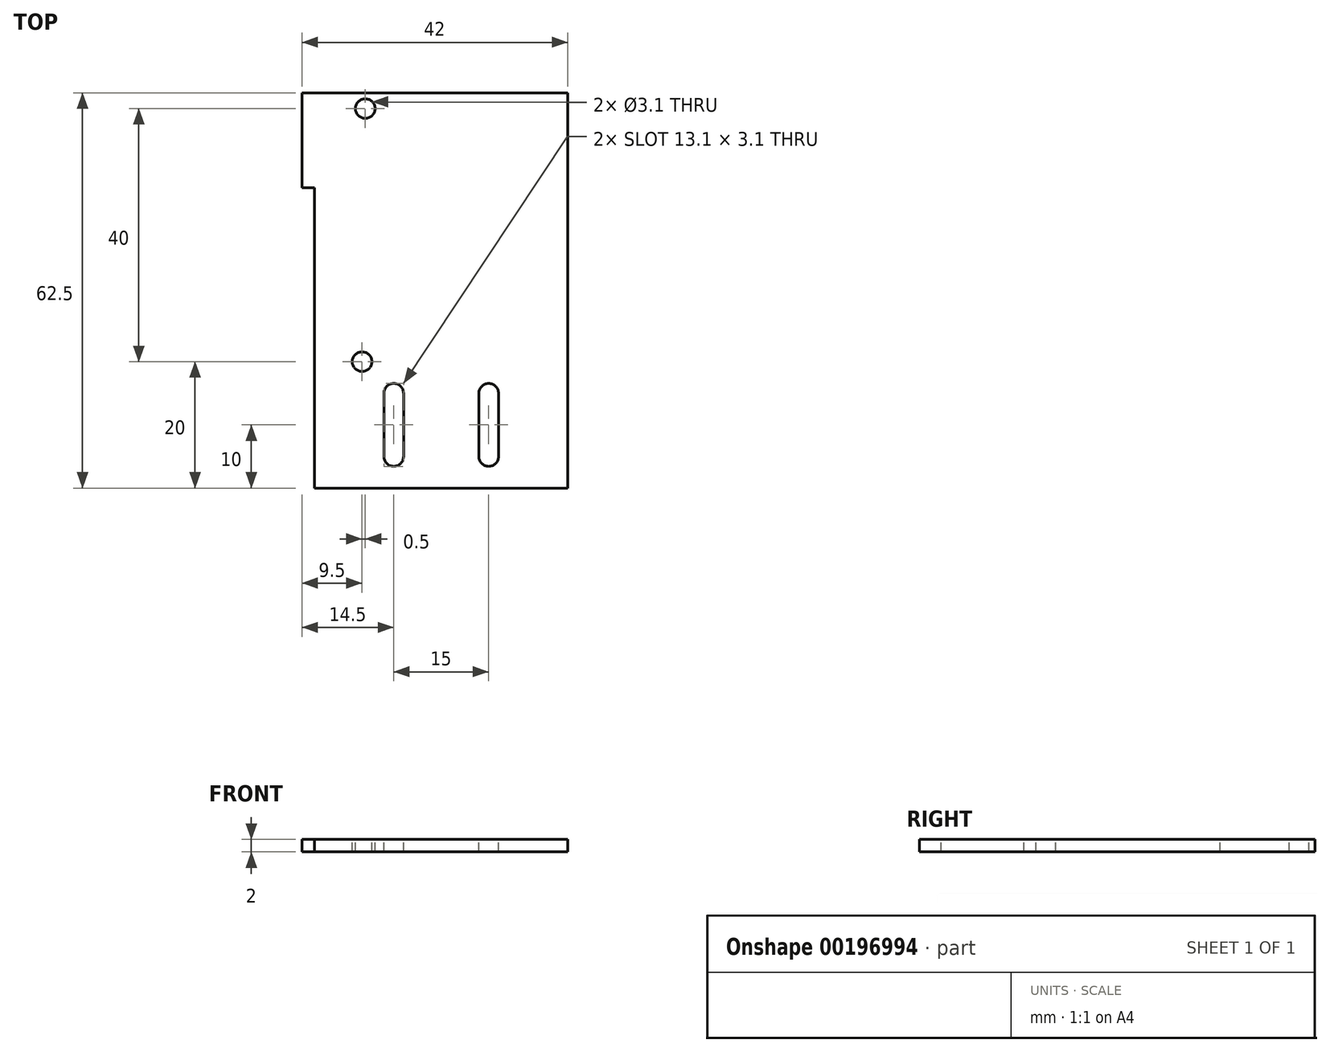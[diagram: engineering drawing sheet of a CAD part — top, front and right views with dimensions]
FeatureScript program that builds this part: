
annotation { "Feature Type Name" : "Feature", "Feature Type Description" : "" }
export const myFeature = defineFeature(function(context is Context, id is Id, definition is map)
    precondition{}
    {
        {
            var Q0;
            Q0=qCreatedBy(makeId("Top.planeOp"),FACE);
            var sketch = newSketch(context, id + "F0", { "sketchPlane" : qUnion([Q0])});
            skLineSegment(sketch, "E0.bottom", {"start": v(20, 32.5) * mm, "end": v(-20, 32.5) * mm});
            skLineSegment(sketch, "E0.top", {"start": v(20, -32.5) * mm, "end": v(-20, -32.5) * mm});
            skLineSegment(sketch, "E0.left", {"start": v(20, 32.5) * mm, "end": v(20, -32.5) * mm});
            skLineSegment(sketch, "E0.right", {"start": v(-20, 32.5) * mm, "end": v(-20, -32.5) * mm});
            skPoint(sketch, "E0.middle", {"position": v(0, 0) * mm});
            skSolve(sketch);
        }
        {
            var Q0;
            Q0 = qSketchRegion(id + "F0", true);
            extrude(context, id + "F1", {"entities" : qUnion([Q0]), "depth" : 2 * mm});
        }
        {
            var Q0;
            Q0=makeQuery(id+"F1.opExtrude","CAP_FACE",FACE,{"disambiguationData":[OSD([sQuery(id+"F0.wireOp",EDGE,"E0.bottom"),sQuery(id+"F0.wireOp",EDGE,"E0.top"),sQuery(id+"F0.wireOp",EDGE,"E0.left"),sQuery(id+"F0.wireOp",EDGE,"E0.right")])],"isStart":false});
            var sketch = newSketch(context, id + "F2", { "sketchPlane" : qUnion([Q0])});
            skLineSegment(sketch, "E1", {"start": v(0, 0) * mm, "end": v(0, 20) * mm, "construction": true});
            skLineSegment(sketch, "E2", {"start": v(0, 20) * mm, "end": v(-20, 20) * mm, "construction": true});
            skLineSegment(sketch, "E3.bottom", {"start": v(-20, 12.5) * mm, "end": v(-22, 12.5) * mm});
            skLineSegment(sketch, "E3.top", {"start": v(-20, 27.5) * mm, "end": v(-22, 27.5) * mm});
            skLineSegment(sketch, "E3.left", {"start": v(-20, 12.5) * mm, "end": v(-20, 27.5) * mm});
            skLineSegment(sketch, "E3.right", {"start": v(-22, 12.5) * mm, "end": v(-22, 27.5) * mm});
            skSolve(sketch);
        }
        {
            var Q0;
            Q0 = qSketchRegion(id + "F2", true);
            extrude(context, id + "F3", {"entities" : qUnion([Q0]), "operationType" : NewBodyOperationType.ADD, "oppositeDirection" : true, "depth" : 2 * mm});
        }
        {
            var Q0;
            {var subQ0=sQuery(id+"F2.wireOp",EDGE,"E3.right");var subQ1=sQuery(id+"F2.wireOp",EDGE,"E3.left");var subQ2=sQuery(id+"F2.wireOp",EDGE,"E3.top");var subQ3=sQuery(id+"F2.wireOp",EDGE,"E3.bottom");Q0=makeQuery(id+"FAu347zrFNA7xFl_1.1.FN0kvEoHNVdJmEl_1.1.F3.boolean.opBoolean","MERGE",FACE,{"derivedFrom":[makeQuery(id+"FAu347zrFNA7xFl_1.1.F3.boolean.opBoolean","MERGE",FACE,{"derivedFrom":[makeQuery(id+"FN0kvEoHNVdJmEl_1.1.F3.boolean.opBoolean","MERGE",FACE,{"derivedFrom":[makeQuery(id+"F3.boolean.opBoolean","MERGE",FACE,{"derivedFrom":[makeQuery(id+"F1.opExtrude","CAP_FACE",FACE,{"disambiguationData":[OSD([sQuery(id+"F0.wireOp",EDGE,"E0.bottom"),sQuery(id+"F0.wireOp",EDGE,"E0.top"),sQuery(id+"F0.wireOp",EDGE,"E0.left"),sQuery(id+"F0.wireOp",EDGE,"E0.right")])],"isStart":false}),makeQuery(id+"F3.opExtrude","CAP_FACE",FACE,{"disambiguationData":[OSD([subQ3,subQ2,subQ1,subQ0])],"isStart":true})]}),makeQuery(id+"FN0kvEoHNVdJmEl_1.1.F3.opExtrude","CAP_FACE",FACE,{"disambiguationData":[OSD([subQ3,subQ2,subQ1,subQ0])],"isStart":true})]}),makeQuery(id+"FAu347zrFNA7xFl_1.1.F3.opExtrude","CAP_FACE",FACE,{"disambiguationData":[OSD([subQ3,subQ2,subQ1,subQ0])],"isStart":true})]}),makeQuery(id+"FAu347zrFNA7xFl_1.1.FN0kvEoHNVdJmEl_1.1.F3.opExtrude","CAP_FACE",FACE,{"disambiguationData":[OSD([subQ3,subQ2,subQ1,subQ0])],"isStart":true})]});}
            var sketch = newSketch(context, id + "F4", { "sketchPlane" : qUnion([Q0])});
            skLineSegment(sketch, "E4", {"start": v(0, 0) * mm, "end": v(0, 25) * mm, "construction": true});
            skLineSegment(sketch, "E5", {"start": v(0, 25) * mm, "end": v(-12, 25) * mm, "construction": true});
            skCircle(sketch, "E6", {"center": v(-12, 25) * mm, "radius": 1.55 * mm});
            skSolve(sketch);
        }
        {
            var Q0;
            Q0 = qSketchRegion(id + "F4", true);
            extrude(context, id + "F5", {"entities" : qUnion([Q0]), "operationType" : NewBodyOperationType.REMOVE, "endBound" : BoundingType.THROUGH_ALL, "oppositeDirection" : true, "depth" : 25 * mm});
        }
        {
            var Q0;
            {var subQ0=sQuery(id+"F2.wireOp",EDGE,"E3.right");var subQ1=sQuery(id+"F2.wireOp",EDGE,"E3.left");var subQ2=sQuery(id+"F2.wireOp",EDGE,"E3.top");var subQ3=sQuery(id+"F2.wireOp",EDGE,"E3.bottom");Q0=makeQuery(id+"FAu347zrFNA7xFl_1.1.FN0kvEoHNVdJmEl_1.1.F3.boolean.opBoolean","MERGE",FACE,{"derivedFrom":[makeQuery(id+"FAu347zrFNA7xFl_1.1.F3.boolean.opBoolean","MERGE",FACE,{"derivedFrom":[makeQuery(id+"FN0kvEoHNVdJmEl_1.1.F3.boolean.opBoolean","MERGE",FACE,{"derivedFrom":[makeQuery(id+"F3.boolean.opBoolean","MERGE",FACE,{"derivedFrom":[makeQuery(id+"F1.opExtrude","CAP_FACE",FACE,{"disambiguationData":[OSD([sQuery(id+"F0.wireOp",EDGE,"E0.bottom"),sQuery(id+"F0.wireOp",EDGE,"E0.top"),sQuery(id+"F0.wireOp",EDGE,"E0.left"),sQuery(id+"F0.wireOp",EDGE,"E0.right")])],"isStart":false}),makeQuery(id+"F3.opExtrude","CAP_FACE",FACE,{"disambiguationData":[OSD([subQ3,subQ2,subQ1,subQ0])],"isStart":true})]}),makeQuery(id+"FN0kvEoHNVdJmEl_1.1.F3.opExtrude","CAP_FACE",FACE,{"disambiguationData":[OSD([subQ3,subQ2,subQ1,subQ0])],"isStart":true})]}),makeQuery(id+"FAu347zrFNA7xFl_1.1.F3.opExtrude","CAP_FACE",FACE,{"disambiguationData":[OSD([subQ3,subQ2,subQ1,subQ0])],"isStart":true})]}),makeQuery(id+"FAu347zrFNA7xFl_1.1.FN0kvEoHNVdJmEl_1.1.F3.opExtrude","CAP_FACE",FACE,{"disambiguationData":[OSD([subQ3,subQ2,subQ1,subQ0])],"isStart":true})]});}
            var sketch = newSketch(context, id + "F6", { "sketchPlane" : qUnion([Q0])});
            skLineSegment(sketch, "E7", {"start": v(0, 0) * mm, "end": v(0, -30) * mm, "construction": true});
            skLineSegment(sketch, "E8", {"start": v(0, -30) * mm, "end": v(7.5, -30) * mm, "construction": true});
            skLineSegment(sketch, "E9", {"start": v(0, -30) * mm, "end": v(-7.5, -30) * mm, "construction": true});
            skArc(sketch, "E10", {"start": v(-9.05, -30) * mm, "mid": v(-7.5, -31.55) * mm, "end": v(-5.95, -30) * mm});
            skArc(sketch, "E11", {"start": v(5.95, -30) * mm, "mid": v(7.5, -31.55) * mm, "end": v(9.05, -30) * mm});
            skLineSegment(sketch, "E12", {"start": v(-7.5, -30) * mm, "end": v(-7.5, -20) * mm, "construction": true});
            skLineSegment(sketch, "E13", {"start": v(7.5, -30) * mm, "end": v(7.5, -20) * mm, "construction": true});
            skArc(sketch, "E14", {"start": v(9.05, -20) * mm, "mid": v(7.5, -18.45) * mm, "end": v(5.95, -20) * mm});
            skArc(sketch, "E15", {"start": v(-5.95, -20) * mm, "mid": v(-7.5, -18.45) * mm, "end": v(-9.05, -20) * mm});
            skLineSegment(sketch, "E16", {"start": v(-5.95, -20) * mm, "end": v(-9.05, -20) * mm, "construction": true});
            skLineSegment(sketch, "E17", {"start": v(5.95, -20) * mm, "end": v(9.05, -20) * mm, "construction": true});
            skLineSegment(sketch, "E18", {"start": v(9.05, -30) * mm, "end": v(7.5, -30) * mm, "construction": true});
            skLineSegment(sketch, "E19", {"start": v(-7.5, -30) * mm, "end": v(-9.05, -30) * mm, "construction": true});
            skLineSegment(sketch, "E20", {"start": v(-9.05, -20) * mm, "end": v(-9.05, -30) * mm});
            skLineSegment(sketch, "E21", {"start": v(-7.5, -30) * mm, "end": v(-5.95, -30) * mm, "construction": true});
            skLineSegment(sketch, "E22", {"start": v(7.5, -30) * mm, "end": v(5.95, -30) * mm, "construction": true});
            skLineSegment(sketch, "E23", {"start": v(5.95, -20) * mm, "end": v(5.95, -30) * mm});
            skLineSegment(sketch, "E24", {"start": v(9.05, -20) * mm, "end": v(9.05, -30) * mm});
            skLineSegment(sketch, "E25", {"start": v(-5.95, -20) * mm, "end": v(-5.95, -30) * mm});
            skSolve(sketch);
        }
        {
            var Q0;
            Q0 = qSketchRegion(id + "F6", true);
            extrude(context, id + "F7", {"entities" : qUnion([Q0]), "operationType" : NewBodyOperationType.REMOVE, "endBound" : BoundingType.THROUGH_ALL, "oppositeDirection" : true, "depth" : 25 * mm});
        }
        {
            var Q0;
            {var subQ0=sQuery(id+"F2.wireOp",EDGE,"E3.right");var subQ1=sQuery(id+"F2.wireOp",EDGE,"E3.left");var subQ2=sQuery(id+"F2.wireOp",EDGE,"E3.top");var subQ3=sQuery(id+"F2.wireOp",EDGE,"E3.bottom");Q0=makeQuery(id+"FAu347zrFNA7xFl_1.1.FN0kvEoHNVdJmEl_1.1.F3.boolean.opBoolean","MERGE",FACE,{"derivedFrom":[makeQuery(id+"FAu347zrFNA7xFl_1.1.F3.boolean.opBoolean","MERGE",FACE,{"derivedFrom":[makeQuery(id+"FN0kvEoHNVdJmEl_1.1.F3.boolean.opBoolean","MERGE",FACE,{"derivedFrom":[makeQuery(id+"F3.boolean.opBoolean","MERGE",FACE,{"derivedFrom":[makeQuery(id+"F1.opExtrude","CAP_FACE",FACE,{"disambiguationData":[OSD([sQuery(id+"F0.wireOp",EDGE,"E0.bottom"),sQuery(id+"F0.wireOp",EDGE,"E0.top"),sQuery(id+"F0.wireOp",EDGE,"E0.left"),sQuery(id+"F0.wireOp",EDGE,"E0.right")])],"isStart":false}),makeQuery(id+"F3.opExtrude","CAP_FACE",FACE,{"disambiguationData":[OSD([subQ3,subQ2,subQ1,subQ0])],"isStart":true})]}),makeQuery(id+"FN0kvEoHNVdJmEl_1.1.F3.opExtrude","CAP_FACE",FACE,{"disambiguationData":[OSD([subQ3,subQ2,subQ1,subQ0])],"isStart":true})]}),makeQuery(id+"FAu347zrFNA7xFl_1.1.F3.opExtrude","CAP_FACE",FACE,{"disambiguationData":[OSD([subQ3,subQ2,subQ1,subQ0])],"isStart":true})]}),makeQuery(id+"FAu347zrFNA7xFl_1.1.FN0kvEoHNVdJmEl_1.1.F3.opExtrude","CAP_FACE",FACE,{"disambiguationData":[OSD([subQ3,subQ2,subQ1,subQ0])],"isStart":true})]});}
            var sketch = newSketch(context, id + "F8", { "sketchPlane" : qUnion([Q0])});
            skLineSegment(sketch, "E26.bottom", {"start": v(-20, -32.5) * mm, "end": v(20, -32.5) * mm});
            skLineSegment(sketch, "E26.top", {"start": v(-20, -35) * mm, "end": v(20, -35) * mm});
            skLineSegment(sketch, "E26.left", {"start": v(-20, -32.5) * mm, "end": v(-20, -35) * mm});
            skLineSegment(sketch, "E26.right", {"start": v(20, -32.5) * mm, "end": v(20, -35) * mm});
            skSolve(sketch);
        }
        {
            var Q0;
            Q0 = qSketchRegion(id + "F8", true);
            var Q1;
            {var subQ0=sQuery(id+"F2.wireOp",EDGE,"E3.right");var subQ1=sQuery(id+"F2.wireOp",EDGE,"E3.left");var subQ2=sQuery(id+"F2.wireOp",EDGE,"E3.top");var subQ3=sQuery(id+"F2.wireOp",EDGE,"E3.bottom");Q1=makeQuery(id+"FAu347zrFNA7xFl_1.1.FN0kvEoHNVdJmEl_1.1.F3.boolean.opBoolean","MERGE",FACE,{"derivedFrom":[makeQuery(id+"FAu347zrFNA7xFl_1.1.F3.boolean.opBoolean","MERGE",FACE,{"derivedFrom":[makeQuery(id+"FN0kvEoHNVdJmEl_1.1.F3.boolean.opBoolean","MERGE",FACE,{"derivedFrom":[makeQuery(id+"F3.boolean.opBoolean","MERGE",FACE,{"derivedFrom":[makeQuery(id+"F1.opExtrude","CAP_FACE",FACE,{"disambiguationData":[OSD([sQuery(id+"F0.wireOp",EDGE,"E0.bottom"),sQuery(id+"F0.wireOp",EDGE,"E0.top"),sQuery(id+"F0.wireOp",EDGE,"E0.left"),sQuery(id+"F0.wireOp",EDGE,"E0.right")])],"isStart":true}),makeQuery(id+"F3.opExtrude","CAP_FACE",FACE,{"disambiguationData":[OSD([subQ3,subQ2,subQ1,subQ0])],"isStart":false})]}),makeQuery(id+"FN0kvEoHNVdJmEl_1.1.F3.opExtrude","CAP_FACE",FACE,{"disambiguationData":[OSD([subQ3,subQ2,subQ1,subQ0])],"isStart":false})]}),makeQuery(id+"FAu347zrFNA7xFl_1.1.F3.opExtrude","CAP_FACE",FACE,{"disambiguationData":[OSD([subQ3,subQ2,subQ1,subQ0])],"isStart":false})]}),makeQuery(id+"FAu347zrFNA7xFl_1.1.FN0kvEoHNVdJmEl_1.1.F3.opExtrude","CAP_FACE",FACE,{"disambiguationData":[OSD([subQ3,subQ2,subQ1,subQ0])],"isStart":false})]});}
            extrude(context, id + "F9", {"entities" : qUnion([Q0]), "operationType" : NewBodyOperationType.ADD, "endBound" : BoundingType.UP_TO_SURFACE, "oppositeDirection" : true, "endBoundEntityFace" : qUnion([Q1]), "depth" : 2 * mm});
        }
        {
            var Q0;
            {var subQ0=sQuery(id+"F2.wireOp",EDGE,"E3.right");var subQ1=sQuery(id+"F2.wireOp",EDGE,"E3.left");var subQ2=sQuery(id+"F2.wireOp",EDGE,"E3.top");var subQ3=sQuery(id+"F2.wireOp",EDGE,"E3.bottom");Q0=makeQuery(id+"F9.boolean.opBoolean","MERGE",FACE,{"derivedFrom":[makeQuery(id+"FAu347zrFNA7xFl_1.1.FN0kvEoHNVdJmEl_1.1.F3.boolean.opBoolean","MERGE",FACE,{"derivedFrom":[makeQuery(id+"FAu347zrFNA7xFl_1.1.F3.boolean.opBoolean","MERGE",FACE,{"derivedFrom":[makeQuery(id+"FN0kvEoHNVdJmEl_1.1.F3.boolean.opBoolean","MERGE",FACE,{"derivedFrom":[makeQuery(id+"F3.boolean.opBoolean","MERGE",FACE,{"derivedFrom":[makeQuery(id+"F1.opExtrude","CAP_FACE",FACE,{"disambiguationData":[OSD([sQuery(id+"F0.wireOp",EDGE,"E0.bottom"),sQuery(id+"F0.wireOp",EDGE,"E0.top"),sQuery(id+"F0.wireOp",EDGE,"E0.left"),sQuery(id+"F0.wireOp",EDGE,"E0.right")])],"isStart":false}),makeQuery(id+"F3.opExtrude","CAP_FACE",FACE,{"disambiguationData":[OSD([subQ3,subQ2,subQ1,subQ0])],"isStart":true})]}),makeQuery(id+"FN0kvEoHNVdJmEl_1.1.F3.opExtrude","CAP_FACE",FACE,{"disambiguationData":[OSD([subQ3,subQ2,subQ1,subQ0])],"isStart":true})]}),makeQuery(id+"FAu347zrFNA7xFl_1.1.F3.opExtrude","CAP_FACE",FACE,{"disambiguationData":[OSD([subQ3,subQ2,subQ1,subQ0])],"isStart":true})]}),makeQuery(id+"FAu347zrFNA7xFl_1.1.FN0kvEoHNVdJmEl_1.1.F3.opExtrude","CAP_FACE",FACE,{"disambiguationData":[OSD([subQ3,subQ2,subQ1,subQ0])],"isStart":true})]}),makeQuery(id+"F9.opExtrude","CAP_FACE",FACE,{"disambiguationData":[OSD([sQuery(id+"F8.wireOp",EDGE,"E26.bottom"),sQuery(id+"F8.wireOp",EDGE,"E26.top"),sQuery(id+"F8.wireOp",EDGE,"E26.left"),sQuery(id+"F8.wireOp",EDGE,"E26.right")])],"isStart":true})]});}
            var sketch = newSketch(context, id + "F10", { "sketchPlane" : qUnion([Q0])});
            skCircle(sketch, "E27", {"center": v(-12.5, -15) * mm, "radius": 1.55 * mm});
            skLineSegment(sketch, "E28", {"start": v(-12.5, -15) * mm, "end": v(0, -15) * mm, "construction": true});
            skLineSegment(sketch, "E29", {"start": v(0, -15) * mm, "end": v(0, 0) * mm, "construction": true});
            skSolve(sketch);
        }
        {
            var Q0;
            Q0 = qSketchRegion(id + "F10", true);
            extrude(context, id + "F11", {"entities" : qUnion([Q0]), "operationType" : NewBodyOperationType.REMOVE, "endBound" : BoundingType.THROUGH_ALL, "oppositeDirection" : true, "depth" : 25 * mm});
        }
        {
            var Q0;
            {var subQ0=sQuery(id+"F2.wireOp",EDGE,"E3.right");var subQ1=sQuery(id+"F2.wireOp",EDGE,"E3.left");var subQ2=sQuery(id+"F2.wireOp",EDGE,"E3.top");var subQ3=sQuery(id+"F2.wireOp",EDGE,"E3.bottom");Q0=makeQuery(id+"F9.boolean.opBoolean","MERGE",FACE,{"derivedFrom":[makeQuery(id+"FAu347zrFNA7xFl_1.1.FN0kvEoHNVdJmEl_1.1.F3.boolean.opBoolean","MERGE",FACE,{"derivedFrom":[makeQuery(id+"FAu347zrFNA7xFl_1.1.F3.boolean.opBoolean","MERGE",FACE,{"derivedFrom":[makeQuery(id+"FN0kvEoHNVdJmEl_1.1.F3.boolean.opBoolean","MERGE",FACE,{"derivedFrom":[makeQuery(id+"F3.boolean.opBoolean","MERGE",FACE,{"derivedFrom":[makeQuery(id+"F1.opExtrude","CAP_FACE",FACE,{"disambiguationData":[OSD([sQuery(id+"F0.wireOp",EDGE,"E0.bottom"),sQuery(id+"F0.wireOp",EDGE,"E0.top"),sQuery(id+"F0.wireOp",EDGE,"E0.left"),sQuery(id+"F0.wireOp",EDGE,"E0.right")])],"isStart":false}),makeQuery(id+"F3.opExtrude","CAP_FACE",FACE,{"disambiguationData":[OSD([subQ3,subQ2,subQ1,subQ0])],"isStart":true})]}),makeQuery(id+"FN0kvEoHNVdJmEl_1.1.F3.opExtrude","CAP_FACE",FACE,{"disambiguationData":[OSD([subQ3,subQ2,subQ1,subQ0])],"isStart":true})]}),makeQuery(id+"FAu347zrFNA7xFl_1.1.F3.opExtrude","CAP_FACE",FACE,{"disambiguationData":[OSD([subQ3,subQ2,subQ1,subQ0])],"isStart":true})]}),makeQuery(id+"FAu347zrFNA7xFl_1.1.FN0kvEoHNVdJmEl_1.1.F3.opExtrude","CAP_FACE",FACE,{"disambiguationData":[OSD([subQ3,subQ2,subQ1,subQ0])],"isStart":true})]}),makeQuery(id+"F9.opExtrude","CAP_FACE",FACE,{"disambiguationData":[OSD([sQuery(id+"F8.wireOp",EDGE,"E26.bottom"),sQuery(id+"F8.wireOp",EDGE,"E26.top"),sQuery(id+"F8.wireOp",EDGE,"E26.left"),sQuery(id+"F8.wireOp",EDGE,"E26.right")])],"isStart":true})]});}
            var sketch = newSketch(context, id + "F12", { "sketchPlane" : qUnion([Q0])});
            skLineSegment(sketch, "E30.bottom", {"start": v(-20, 27.5) * mm, "end": v(20, 27.5) * mm});
            skLineSegment(sketch, "E30.top", {"start": v(-20, 32.5) * mm, "end": v(20, 32.5) * mm});
            skLineSegment(sketch, "E30.left", {"start": v(-20, 27.5) * mm, "end": v(-20, 32.5) * mm});
            skLineSegment(sketch, "E30.right", {"start": v(20, 27.5) * mm, "end": v(20, 32.5) * mm});
            skSolve(sketch);
        }
        {
            var Q0;
            Q0 = qSketchRegion(id + "F12", true);
            extrude(context, id + "F13", {"entities" : qUnion([Q0]), "operationType" : NewBodyOperationType.REMOVE, "oppositeDirection" : true, "depth" : 25 * mm});
        }
    });
